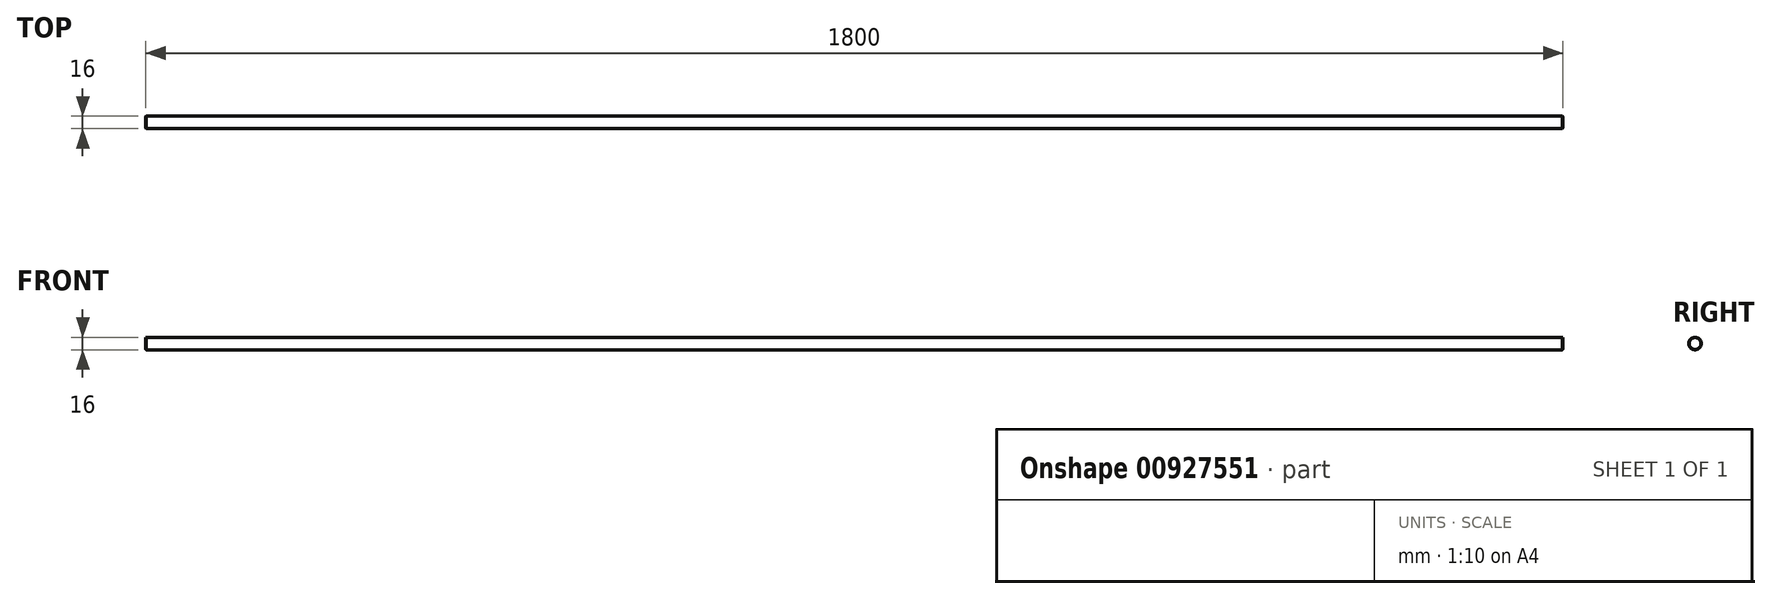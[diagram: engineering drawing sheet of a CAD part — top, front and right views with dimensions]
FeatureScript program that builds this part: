
annotation { "Feature Type Name" : "Feature", "Feature Type Description" : "" }
export const myFeature = defineFeature(function(context is Context, id is Id, definition is map)
    precondition{}
    {
        {
            var Q0;
            Q0=qCreatedBy(makeId("Right.planeOp"),FACE);
            var sketch = newSketch(context, id + "F0", { "sketchPlane" : qUnion([Q0])});
            skCircle(sketch, "E0", {"center": v(0, 0) * mm, "radius": 8 * mm});
            skSolve(sketch);
        }
        {
            var Q0;
            Q0 = qSketchRegion(id + "F0", true);
            extrude(context, id + "F1", {"entities" : qUnion([Q0]), "oppositeDirection" : true, "depth" : 1800 * mm, "offsetDistance" : 25 * mm});
        }
        {
            var Q0;
            Q0=makeQuery(id+"F1.opExtrude","CAP_EDGE",EDGE,{"disambiguationData":[OSD([sQuery(id+"F0.wireOp",EDGE,"E0")])],"isStart":true});
            var Q1;
            Q1=makeQuery(id+"F1.opExtrude","CAP_EDGE",EDGE,{"disambiguationData":[OSD([sQuery(id+"F0.wireOp",EDGE,"E0")])],"isStart":false});
            chamfer(context, id + "F2", {"entities" : qUnion([Q0, Q1]), "width" : 0.5 * mm, "tangentPropagation" : true});
        }
    });
